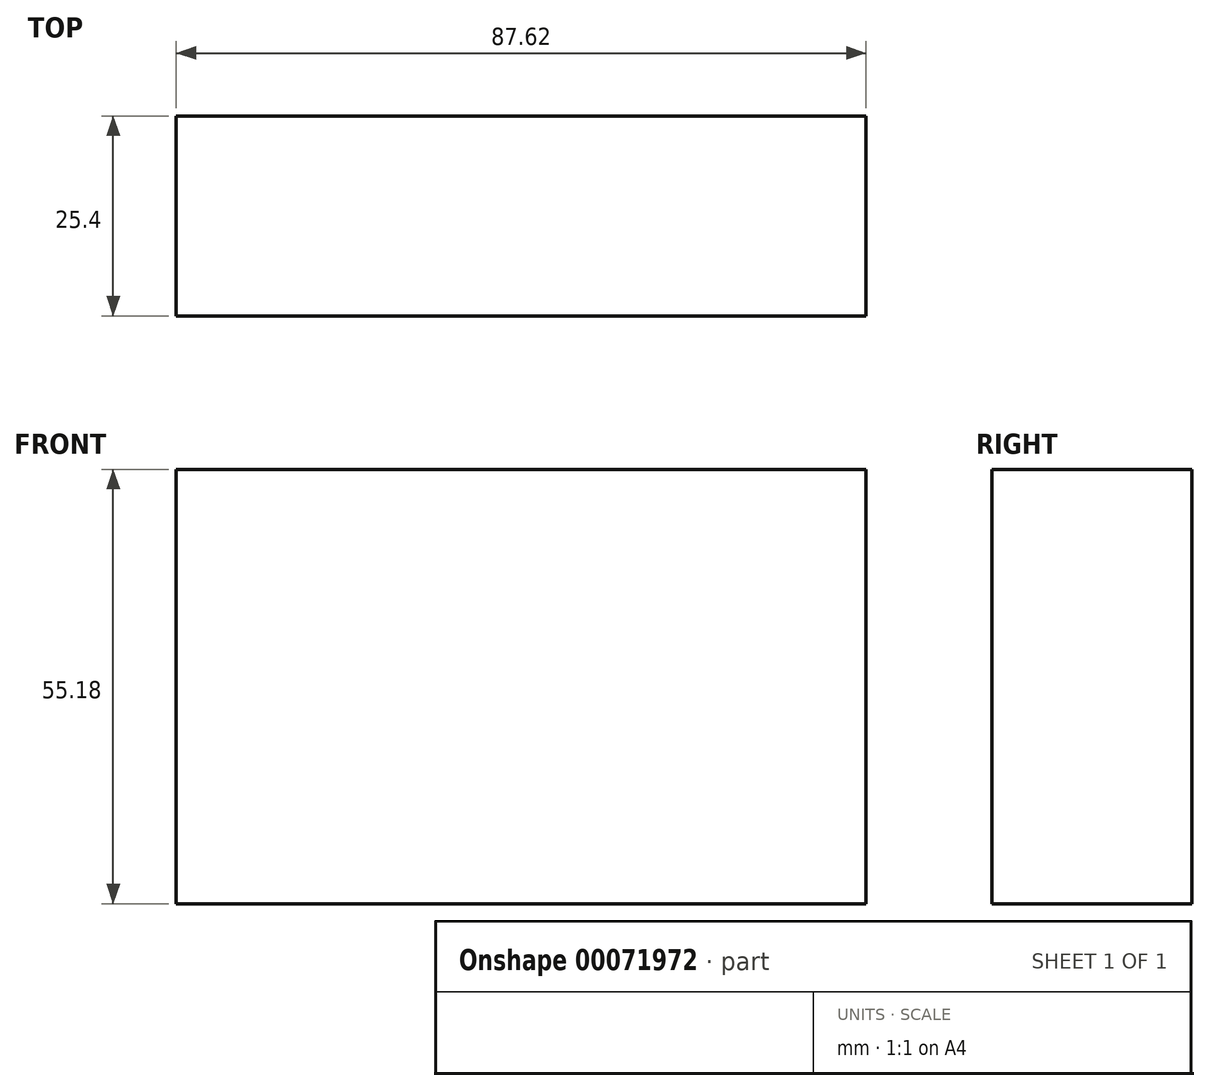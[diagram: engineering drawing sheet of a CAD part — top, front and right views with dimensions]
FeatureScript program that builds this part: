
annotation { "Feature Type Name" : "Feature", "Feature Type Description" : "" }
export const myFeature = defineFeature(function(context is Context, id is Id, definition is map)
    precondition{}
    {
        {
            var Q0;
            Q0=qCreatedBy(makeId("Front.planeOp"),FACE);
            var sketch = newSketch(context, id + "F0", { "sketchPlane" : qUnion([Q0])});
            skLineSegment(sketch, "E0.bottom", {"start": v(-43.8, 27.59) * mm, "end": v(43.8, 27.59) * mm});
            skLineSegment(sketch, "E0.top", {"start": v(-43.8, -27.59) * mm, "end": v(43.8, -27.59) * mm});
            skLineSegment(sketch, "E0.left", {"start": v(-43.8, 27.59) * mm, "end": v(-43.8, -27.59) * mm});
            skLineSegment(sketch, "E0.right", {"start": v(43.8, 27.59) * mm, "end": v(43.8, -27.59) * mm});
            skSolve(sketch);
        }
        {
            var Q0;
            Q0=makeQuery(id+"F0.imprint","IMPRINT",FACE,{"disambiguationData":[TD([[makeQuery(id+"F0.imprint","IMPRINT",EDGE,{"derivedFrom":sQuery(id+"F0.wireOp",EDGE,"E0.bottom")}),-1.0]])]});
            extrude(context, id + "F1", {"entities" : qUnion([Q0]), "depth" : 25.4 * mm});
        }
    });
